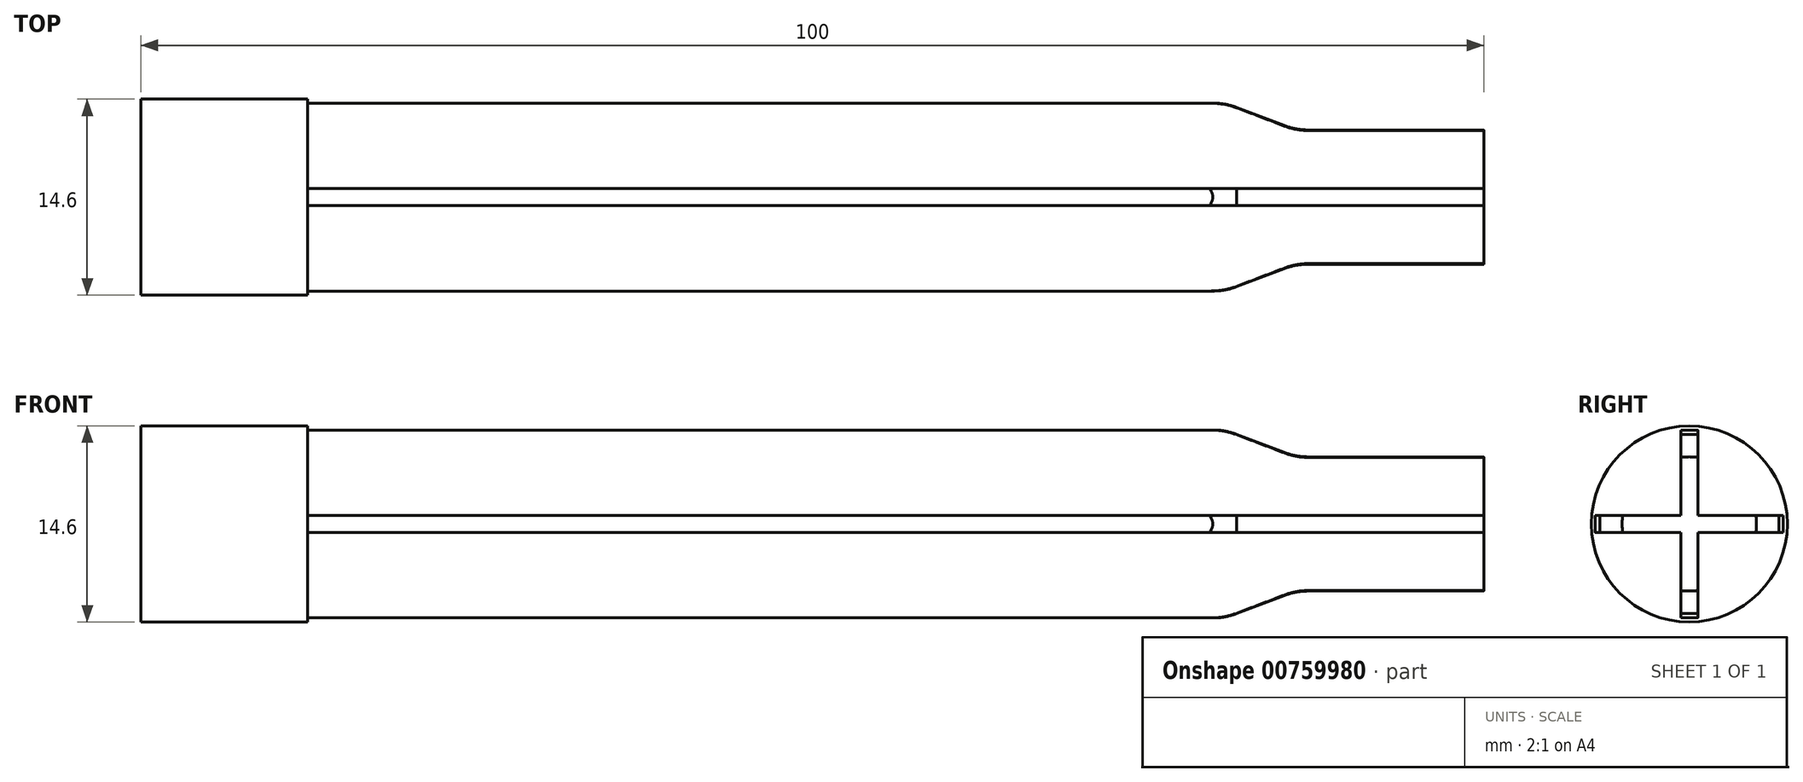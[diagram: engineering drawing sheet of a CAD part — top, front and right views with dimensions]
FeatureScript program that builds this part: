
annotation { "Feature Type Name" : "Feature", "Feature Type Description" : "" }
export const myFeature = defineFeature(function(context is Context, id is Id, definition is map)
    precondition{}
    {
        {
            var Q0;
            Q0=qCreatedBy(makeId("Right.planeOp"),FACE);
            var sketch = newSketch(context, id + "F0", { "sketchPlane" : qUnion([Q0])});
            skCircle(sketch, "E0", {"center": v(0, 0) * mm, "radius": 7.3 * mm});
            skSolve(sketch);
        }
        {
            var Q0;
            Q0=makeQuery(id+"F0.imprint","IMPRINT",FACE,{"disambiguationData":[TD([[makeQuery(id+"F0.imprint","IMPRINT",EDGE,{"derivedFrom":sQuery(id+"F0.wireOp",EDGE,"E0")}),1.0]])]});
            extrude(context, id + "F1", {"entities" : qUnion([Q0]), "depth" : 100 * mm, "offsetDistance" : 25.4 * mm});
        }
        {
            var Q0;
            Q0=makeQuery(id+"F1.opExtrude","CAP_FACE",FACE,{"disambiguationData":[OSD([sQuery(id+"F0.wireOp",EDGE,"E0")])],"isStart":false});
            var sketch = newSketch(context, id + "F2", { "sketchPlane" : qUnion([Q0])});
            skLineSegment(sketch, "E1.bottom", {"start": v(-8.26, 8.26) * mm, "end": v(-0.64, 8.26) * mm});
            skLineSegment(sketch, "E1.top", {"start": v(-8.26, 0.63) * mm, "end": v(-0.64, 0.64) * mm});
            skLineSegment(sketch, "E1.left", {"start": v(-8.26, 8.26) * mm, "end": v(-8.26, 0.63) * mm});
            skLineSegment(sketch, "E1.right", {"start": v(-0.64, 8.26) * mm, "end": v(-0.64, 0.64) * mm});
            skLineSegment(sketch, "E2.bottom", {"start": v(0.64, 0.63) * mm, "end": v(8.26, 0.64) * mm});
            skLineSegment(sketch, "E2.top", {"start": v(0.63, 8.26) * mm, "end": v(8.25, 8.26) * mm});
            skLineSegment(sketch, "E2.left", {"start": v(0.64, 0.63) * mm, "end": v(0.63, 8.26) * mm});
            skLineSegment(sketch, "E2.right", {"start": v(8.26, 0.64) * mm, "end": v(8.25, 8.26) * mm});
            skLineSegment(sketch, "E3.bottom", {"start": v(0.64, -0.64) * mm, "end": v(8.26, -0.64) * mm});
            skLineSegment(sketch, "E3.top", {"start": v(0.64, -8.26) * mm, "end": v(8.26, -8.26) * mm});
            skLineSegment(sketch, "E3.left", {"start": v(0.64, -0.64) * mm, "end": v(0.64, -8.26) * mm});
            skLineSegment(sketch, "E3.right", {"start": v(8.26, -0.64) * mm, "end": v(8.26, -8.26) * mm});
            skLineSegment(sketch, "E4.bottom", {"start": v(-0.64, -0.64) * mm, "end": v(-8.26, -0.63) * mm});
            skLineSegment(sketch, "E4.top", {"start": v(-0.63, -8.26) * mm, "end": v(-8.26, -8.26) * mm});
            skLineSegment(sketch, "E4.left", {"start": v(-0.64, -0.64) * mm, "end": v(-0.63, -8.26) * mm});
            skLineSegment(sketch, "E4.right", {"start": v(-8.26, -0.64) * mm, "end": v(-8.26, -8.26) * mm});
            skSolve(sketch);
        }
        {
            var Q0;
            Q0 = qSketchRegion(id + "F2", true);
            extrude(context, id + "F3", {"entities" : qUnion([Q0]), "operationType" : NewBodyOperationType.REMOVE, "oppositeDirection" : true, "depth" : 87.6 * mm, "offsetDistance" : 25.4 * mm});
        }
        {
            var Q0;
            Q0=makeQuery(id+"F1.opExtrude","CAP_FACE",FACE,{"disambiguationData":[OSD([sQuery(id+"F0.wireOp",EDGE,"E0")])],"isStart":false});
            var sketch = newSketch(context, id + "F4", { "sketchPlane" : qUnion([Q0])});
            skLineSegment(sketch, "E5.bottom", {"start": v(7, -7) * mm, "end": v(-7, -7) * mm});
            skLineSegment(sketch, "E5.top", {"start": v(7, 7) * mm, "end": v(-7, 7) * mm});
            skLineSegment(sketch, "E5.left", {"start": v(7, -7) * mm, "end": v(7, 7) * mm});
            skLineSegment(sketch, "E5.right", {"start": v(-7, -7) * mm, "end": v(-7, 7) * mm});
            skPoint(sketch, "E5.middle", {"position": v(0, 0) * mm});
            skLineSegment(sketch, "E6.bottom", {"start": v(10.16, -10.16) * mm, "end": v(-10.16, -10.16) * mm});
            skLineSegment(sketch, "E6.top", {"start": v(10.16, 10.16) * mm, "end": v(-10.16, 10.16) * mm});
            skLineSegment(sketch, "E6.left", {"start": v(10.16, -10.16) * mm, "end": v(10.16, 10.16) * mm});
            skLineSegment(sketch, "E6.right", {"start": v(-10.16, -10.16) * mm, "end": v(-10.16, 10.16) * mm});
            skSolve(sketch);
        }
        {
            var Q0;
            Q0 = qSketchRegion(id + "F4", true);
            var Q1;
            Q1=makeQuery(id+"F3.boolean.opBoolean","COPY",FACE,{"derivedFrom":makeQuery(id+"F3.opExtrude","CAP_FACE",FACE,{"disambiguationData":[OSD([sQuery(id+"F2.wireOp",EDGE,"E1.bottom"),sQuery(id+"F2.wireOp",EDGE,"E1.top"),sQuery(id+"F2.wireOp",EDGE,"E1.left"),sQuery(id+"F2.wireOp",EDGE,"E1.right")])],"isStart":false})});
            extrude(context, id + "F5", {"entities" : qUnion([Q0]), "operationType" : NewBodyOperationType.REMOVE, "endBound" : BoundingType.UP_TO_SURFACE, "oppositeDirection" : true, "depth" : 25.4 * mm, "endBoundEntityFace" : qUnion([Q1]), "offsetDistance" : 25.4 * mm});
        }
        {
            var Q0;
            Q0=qCreatedBy(makeId("Front.planeOp"),FACE);
            var sketch = newSketch(context, id + "F6", { "sketchPlane" : qUnion([Q0])});
            skLineSegment(sketch, "E7", {"start": v(100, 5) * mm, "end": v(86, 5) * mm});
            skLineSegment(sketch, "E8", {"start": v(86, 5) * mm, "end": v(80, 7.28) * mm});
            skLineSegment(sketch, "E9", {"start": v(80, 7.28) * mm, "end": v(100.02, 7.28) * mm});
            skLineSegment(sketch, "E10", {"start": v(72.21, 0) * mm, "end": v(104.12, 0) * mm});
            skLineSegment(sketch, "E11", {"start": v(100, 5) * mm, "end": v(100.02, 7.28) * mm});
            skSolve(sketch);
        }
        {
            var Q0;
            Q0 = qSketchRegion(id + "F6", true);
            var Q1;
            Q1=sQuery(id+"F6.wireOp",EDGE,"E10");
            revolve(context, id + "F7", {"operationType" : NewBodyOperationType.REMOVE, "surfaceOperationType" : NewSurfaceOperationType.NEW, "entities" : qUnion([Q0]), "axis" : qUnion([Q1]), "revolveType" : RevolveType.FULL, "oppositeDirection" : true});
        }
        {
            var Q0;
            Q0=makeQuery(id+"F7.boolean.opBoolean","INTERSECT",EDGE,{"derivedFrom":[makeQuery(id+"F5.boolean.opBoolean","COPY",FACE,{"derivedFrom":makeQuery(id+"F5.opExtrude","SWEPT_FACE",FACE,{"disambiguationData":[OSD([sQuery(id+"F4.wireOp",EDGE,"E5.top")])]})}),makeQuery(id+"F7.opRevolve","SWEPT_FACE",FACE,{"disambiguationData":[OSD([sQuery(id+"F6.wireOp",EDGE,"E8")])]})]});
            var Q1;
            {var subQ0=sQuery(id+"F6.wireOp",EDGE,"E7");var subQ1=sQuery(id+"F6.wireOp",EDGE,"E8");Q1=makeQuery(id+"F7.boolean.opBoolean","COPY",EDGE,{"disambiguationData":[TD([makeQuery(id+"F3.boolean.opBoolean","COPY",FACE,{"derivedFrom":makeQuery(id+"F3.opExtrude","SWEPT_FACE",FACE,{"disambiguationData":[OSD([sQuery(id+"F2.wireOp",EDGE,"E1.right")])]})})])],"derivedFrom":makeQuery(id+"F7.opRevolve","SWEPT_EDGE",EDGE,{"disambiguationData":[OSD([subQ0,subQ1])]})});}
            var Q2;
            {var subQ0=sQuery(id+"F6.wireOp",EDGE,"E7");var subQ1=sQuery(id+"F6.wireOp",EDGE,"E8");Q2=makeQuery(id+"F7.boolean.opBoolean","COPY",EDGE,{"disambiguationData":[TD([makeQuery(id+"F3.boolean.opBoolean","COPY",FACE,{"derivedFrom":makeQuery(id+"F3.opExtrude","SWEPT_FACE",FACE,{"disambiguationData":[OSD([sQuery(id+"F2.wireOp",EDGE,"E1.top")])]})})])],"derivedFrom":makeQuery(id+"F7.opRevolve","SWEPT_EDGE",EDGE,{"disambiguationData":[OSD([subQ0,subQ1])]})});}
            var Q3;
            Q3=makeQuery(id+"F7.boolean.opBoolean","INTERSECT",EDGE,{"derivedFrom":[makeQuery(id+"F5.boolean.opBoolean","COPY",FACE,{"derivedFrom":makeQuery(id+"F5.opExtrude","SWEPT_FACE",FACE,{"disambiguationData":[OSD([sQuery(id+"F4.wireOp",EDGE,"E5.right")])]})}),makeQuery(id+"F7.opRevolve","SWEPT_FACE",FACE,{"disambiguationData":[OSD([sQuery(id+"F6.wireOp",EDGE,"E8")])]})]});
            var Q4;
            Q4=makeQuery(id+"F7.boolean.opBoolean","INTERSECT",EDGE,{"derivedFrom":[makeQuery(id+"F5.boolean.opBoolean","COPY",FACE,{"derivedFrom":makeQuery(id+"F5.opExtrude","SWEPT_FACE",FACE,{"disambiguationData":[OSD([sQuery(id+"F4.wireOp",EDGE,"E5.bottom")])]})}),makeQuery(id+"F7.opRevolve","SWEPT_FACE",FACE,{"disambiguationData":[OSD([sQuery(id+"F6.wireOp",EDGE,"E8")])]})]});
            var Q5;
            {var subQ0=sQuery(id+"F6.wireOp",EDGE,"E8");var subQ1=sQuery(id+"F6.wireOp",EDGE,"E7");Q5=makeQuery(id+"F7.boolean.opBoolean","COPY",EDGE,{"disambiguationData":[TD([makeQuery(id+"F3.boolean.opBoolean","COPY",FACE,{"derivedFrom":makeQuery(id+"F3.opExtrude","SWEPT_FACE",FACE,{"disambiguationData":[OSD([sQuery(id+"F2.wireOp",EDGE,"E3.left")])]})})])],"derivedFrom":makeQuery(id+"F7.opRevolve","SWEPT_EDGE",EDGE,{"disambiguationData":[OSD([subQ1,subQ0])]})});}
            var Q6;
            {var subQ0=sQuery(id+"F6.wireOp",EDGE,"E8");var subQ1=sQuery(id+"F6.wireOp",EDGE,"E7");Q6=makeQuery(id+"F7.boolean.opBoolean","COPY",EDGE,{"disambiguationData":[TD([makeQuery(id+"F3.boolean.opBoolean","COPY",FACE,{"derivedFrom":makeQuery(id+"F3.opExtrude","SWEPT_FACE",FACE,{"disambiguationData":[OSD([sQuery(id+"F2.wireOp",EDGE,"E2.bottom")])]})})])],"derivedFrom":makeQuery(id+"F7.opRevolve","SWEPT_EDGE",EDGE,{"disambiguationData":[OSD([subQ1,subQ0])]})});}
            var Q7;
            Q7=makeQuery(id+"F7.boolean.opBoolean","INTERSECT",EDGE,{"derivedFrom":[makeQuery(id+"F5.boolean.opBoolean","COPY",FACE,{"derivedFrom":makeQuery(id+"F5.opExtrude","SWEPT_FACE",FACE,{"disambiguationData":[OSD([sQuery(id+"F4.wireOp",EDGE,"E5.left")])]})}),makeQuery(id+"F7.opRevolve","SWEPT_FACE",FACE,{"disambiguationData":[OSD([sQuery(id+"F6.wireOp",EDGE,"E8")])]})]});
            fillet(context, id + "F8", {"entities" : qUnion([Q0, Q1, Q2, Q3, Q4, Q5, Q6, Q7]), "radius" : 5 * mm, "tangentPropagation" : true, "allowEdgeOverflow" : false});
        }
    });
